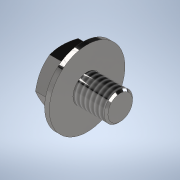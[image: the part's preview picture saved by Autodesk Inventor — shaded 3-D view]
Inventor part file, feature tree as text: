
AUTODESK INVENTOR PART (.ipt)
format: ipt  version: 2020.5 (Build 245400000, 400)  size: 159,744 bytes
history: native  units: in
note: dims shown in document units (in); Inventor stores cm internally (conversion verified against a paired STEP export)
features: sketch x4, extrude x2, revolve x1, chamfer x1, thread x1
ambient origin geometry x8: Origin, YZ Plane, XZ Plane, XY Plane, X Axis, Y Axis, Z Axis, Center Point
bodies: Solid1 (feature_tree)
feature tree (9):
  revolve  "Revolution1"  Angle=30.0deg
  extrude  "Extrusion15"  Depth=0.0197in
  chamfer  "Chamfer5"  Distance=0.1969in
  thread  "Thread7"  [1 undecoded]
  extrude  "Extrusion18"  Depth=0.1575in
  sketch  "Boceto20"  dims[d92=90.0deg d105=0.1969in d106=0.0in d116=0.0886in d117=0.1575in d118=0.0079in d119=0.0787in d120=45.0deg d128=0.1181in d129=0.3937in d130=0.0in d131=0.315in d132=0.0197in d133=0.0in]
  sketch  "Sketch15"  dims[d21=0.7874in d83=30.0deg]
  sketch  "Sketch16"  dims[d84=0.0591in d86=0.0197in]
  sketch  "Sketch19"  dims[d87=0.1181in]
note: 1 required parameter value undecoded (feature->parameter linkage not recoverable at this tier; creation-order binding heuristic only, values carry confidence <= 0.55)
